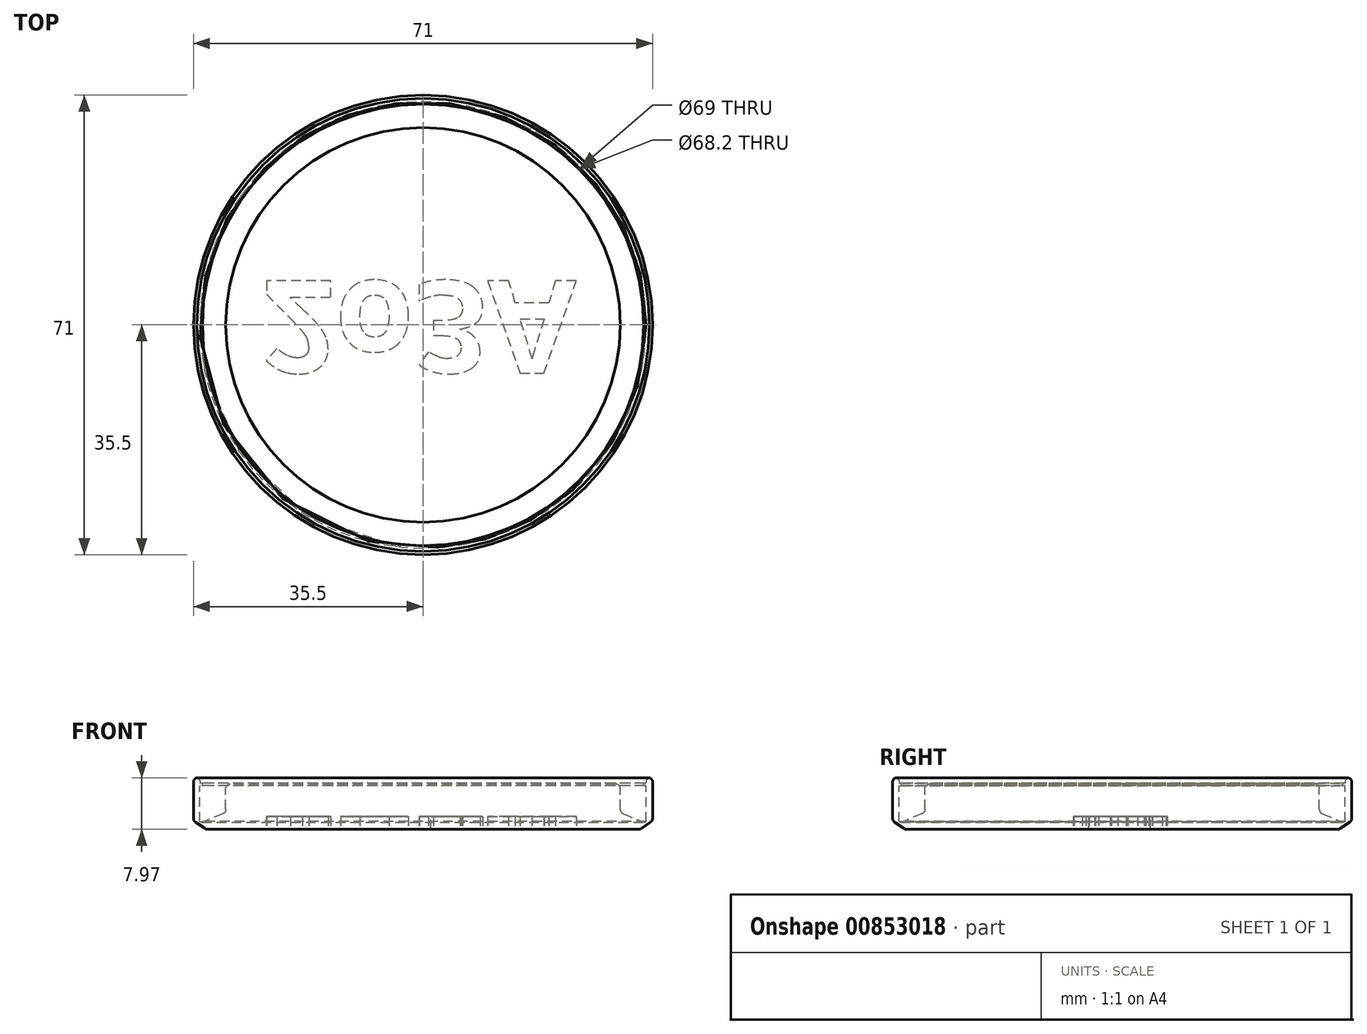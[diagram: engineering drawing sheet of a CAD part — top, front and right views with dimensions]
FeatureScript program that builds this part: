
annotation { "Feature Type Name" : "Feature", "Feature Type Description" : "" }
export const myFeature = defineFeature(function(context is Context, id is Id, definition is map)
    precondition{}
    {
        {
            var Q0;
            Q0=qCreatedBy(makeId("Front.planeOp"),FACE);
            var sketch = newSketch(context, id + "F0", { "sketchPlane" : qUnion([Q0])});
            skLineSegment(sketch, "E0", {"start": v(-35.5, 7.3) * mm, "end": v(-35.5, 1.71) * mm});
            skLineSegment(sketch, "E1", {"start": v(-30.5, 0) * mm, "end": v(0, 0) * mm});
            skLineSegment(sketch, "E2", {"start": v(-35.18, 8) * mm, "end": v(-34.8, 8) * mm});
            skLineSegment(sketch, "E3", {"start": v(0, 2.2) * mm, "end": v(0, 0) * mm});
            skLineSegment(sketch, "E4", {"start": v(-33.93, 1.19) * mm, "end": v(-30.93, 2.43) * mm});
            skLineSegment(sketch, "E5", {"start": v(-30.5, 3.08) * mm, "end": v(-30.5, 6.3) * mm});
            skLineSegment(sketch, "E6", {"start": v(-29.8, 7) * mm, "end": v(0, 7) * mm});
            skLineSegment(sketch, "E7", {"start": v(0, 7) * mm, "end": v(0, 2.2) * mm});
            skLineSegment(sketch, "E8", {"start": v(-35.2, 1.13) * mm, "end": v(-33.71, 0.12) * mm});
            skLineSegment(sketch, "E9", {"start": v(-33.32, 0) * mm, "end": v(-30.5, 0) * mm});
            skPoint(sketch, "E10.visualSharp", {"position": v(-35.5, 8) * mm});
            skArc(sketch, "E10.filletArc", {"start": v(-34.8, 8) * mm, "mid": v(-35.3, 7.8) * mm, "end": v(-35.5, 7.3) * mm});
            skPoint(sketch, "E11.visualSharp", {"position": v(-34.48, 8) * mm});
            skArc(sketch, "E11.filletArc", {"start": v(-34.48, 7.24) * mm, "mid": v(-34.67, 7.77) * mm, "end": v(-35.18, 8) * mm});
            skPoint(sketch, "E12.visualSharp", {"position": v(-35.5, 1.34) * mm});
            skArc(sketch, "E12.filletArc", {"start": v(-35.5, 1.71) * mm, "mid": v(-35.42, 1.38) * mm, "end": v(-35.2, 1.13) * mm});
            skPoint(sketch, "E13.visualSharp", {"position": v(-33.53, 0) * mm});
            skArc(sketch, "E13.filletArc", {"start": v(-33.71, 0.12) * mm, "mid": v(-33.52, 0.03) * mm, "end": v(-33.32, 0) * mm});
            skPoint(sketch, "E14.visualSharp", {"position": v(-33.56, 1.34) * mm});
            skArc(sketch, "E14.filletArc", {"start": v(-34.5, 1.2) * mm, "mid": v(-34.22, 1.13) * mm, "end": v(-33.93, 1.19) * mm});
            skPoint(sketch, "E15.visualSharp", {"position": v(-30.5, 2.61) * mm});
            skArc(sketch, "E15.filletArc", {"start": v(-30.93, 2.43) * mm, "mid": v(-30.62, 2.69) * mm, "end": v(-30.5, 3.08) * mm});
            skPoint(sketch, "E16.visualSharp", {"position": v(-30.5, 7) * mm});
            skArc(sketch, "E16.filletArc", {"start": v(-29.8, 7) * mm, "mid": v(-30.3, 6.8) * mm, "end": v(-30.5, 6.3) * mm});
            skLineSegment(sketch, "E17", {"start": v(-34.4, 7.14) * mm, "end": v(-34.21, 7.14) * mm});
            skLineSegment(sketch, "E18", {"start": v(-34.1, 7.03) * mm, "end": v(-34.1, 6.85) * mm});
            skLineSegment(sketch, "E19", {"start": v(-34.21, 6.74) * mm, "end": v(-34.39, 6.74) * mm});
            skLineSegment(sketch, "E20", {"start": v(-34.5, 6.63) * mm, "end": v(-34.5, 1.2) * mm});
            skPoint(sketch, "E21.visualSharp", {"position": v(-34.1, 6.74) * mm});
            skArc(sketch, "E21.filletArc", {"start": v(-34.21, 6.74) * mm, "mid": v(-34.13, 6.77) * mm, "end": v(-34.1, 6.85) * mm});
            skPoint(sketch, "E22.visualSharp", {"position": v(-34.1, 7.14) * mm});
            skArc(sketch, "E22.filletArc", {"start": v(-34.1, 7.03) * mm, "mid": v(-34.13, 7.1) * mm, "end": v(-34.21, 7.14) * mm});
            skPoint(sketch, "E23.visualSharp", {"position": v(-34.5, 7.14) * mm});
            skArc(sketch, "E23.filletArc", {"start": v(-34.48, 7.24) * mm, "mid": v(-34.46, 7.17) * mm, "end": v(-34.4, 7.14) * mm});
            skPoint(sketch, "E24.visualSharp", {"position": v(-34.5, 6.74) * mm});
            skArc(sketch, "E24.filletArc", {"start": v(-34.39, 6.74) * mm, "mid": v(-34.47, 6.7) * mm, "end": v(-34.5, 6.63) * mm});
            skSolve(sketch);
        }
        {
            var Q0;
            Q0=makeQuery(id+"F0.imprint","IMPRINT",FACE,{"disambiguationData":[TD([[makeQuery(id+"F0.imprint","IMPRINT",EDGE,{"derivedFrom":sQuery(id+"F0.wireOp",EDGE,"E0")}),1.0]])]});
            var Q1;
            Q1=sQuery(id+"F0.wireOp",EDGE,"E3");
            revolve(context, id + "F1", {"surfaceOperationType" : NewSurfaceOperationType.NEW, "entities" : qUnion([Q0]), "axis" : qUnion([Q1]), "revolveType" : RevolveType.FULL});
        }
        {
            var Q0;
            Q0=makeQuery(id+"F1.opRevolve","SWEPT_FACE",FACE,{"disambiguationData":[OSD([sQuery(id+"F0.wireOp",EDGE,"E1"),sQuery(id+"F0.wireOp",EDGE,"E9")])]});
            var sketch = newSketch(context, id + "F2", { "sketchPlane" : qUnion([Q0])});
            skText(sketch, "E25", { "text": "2o3A", "fontName": "OpenSans-Bold.ttf"});
            const initialGuessF2  = {"E25": [-0.025, -0.0068, 1, 0, 0.01431]};
            skSetInitialGuess(sketch, initialGuessF2);
            skSolve(sketch);
        }
        {
            var Q0;
            Q0=qSketchRegion(id+"F2",true);
            extrude(context, id + "F3", {"entities" : qUnion([Q0]), "operationType" : NewBodyOperationType.REMOVE, "oppositeDirection" : true, "depth" : 2 * mm, "offsetDistance" : 25 * mm});
        }
    });
